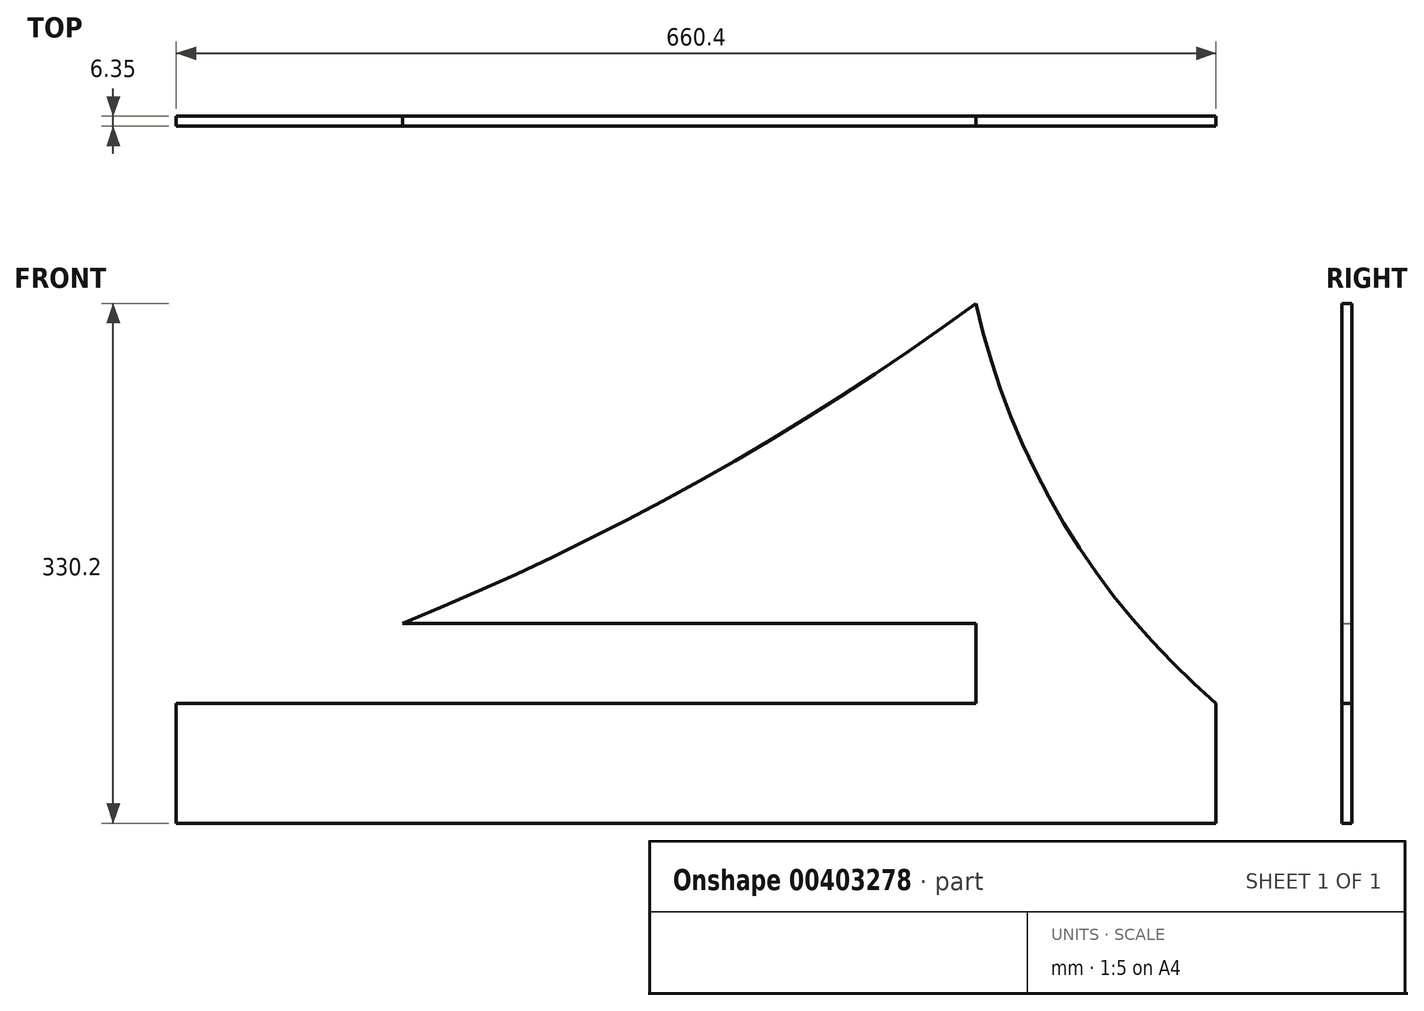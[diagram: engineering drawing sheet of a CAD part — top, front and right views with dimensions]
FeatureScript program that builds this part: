
annotation { "Feature Type Name" : "Feature", "Feature Type Description" : "" }
export const myFeature = defineFeature(function(context is Context, id is Id, definition is map)
    precondition{}
    {
        {
            var Q0;
            Q0=qCreatedBy(makeId("Front.planeOp"),FACE);
            var sketch = newSketch(context, id + "F0", { "sketchPlane" : qUnion([Q0])});
            skLineSegment(sketch, "E0.bottom", {"start": v(0, 0) * mm, "end": v(203.2, 0) * mm});
            skLineSegment(sketch, "E0.top", {"start": v(0, 76.2) * mm, "end": v(203.2, 76.2) * mm});
            skLineSegment(sketch, "E0.left", {"start": v(0, 0) * mm, "end": v(0, 76.2) * mm});
            skLineSegment(sketch, "E0.right", {"start": v(203.2, 0) * mm, "end": v(203.2, 76.2) * mm});
            skLineSegment(sketch, "E1.bottom", {"start": v(0, 0) * mm, "end": v(508, 0) * mm});
            skLineSegment(sketch, "E1.top", {"start": v(0, 254) * mm, "end": v(508, 254) * mm});
            skLineSegment(sketch, "E1.left", {"start": v(0, 0) * mm, "end": v(0, 254) * mm});
            skLineSegment(sketch, "E1.right", {"start": v(508, 0) * mm, "end": v(508, 254) * mm});
            skLineSegment(sketch, "E2.bottom", {"start": v(0, 0) * mm, "end": v(609.6, 0) * mm});
            skLineSegment(sketch, "E2.top", {"start": v(0, 50.8) * mm, "end": v(609.6, 50.8) * mm});
            skLineSegment(sketch, "E2.left", {"start": v(0, 0) * mm, "end": v(0, 50.8) * mm});
            skLineSegment(sketch, "E2.right", {"start": v(609.6, 0) * mm, "end": v(609.6, 50.8) * mm});
            skLineSegment(sketch, "E3", {"start": v(0, 0) * mm, "end": v(660.4, 0) * mm});
            skPoint(sketch, "E3.endSnap0", {"position": v(254, 0) * mm});
            skLineSegment(sketch, "E4.bottom", {"start": v(660.4, 0) * mm, "end": v(0, 0) * mm});
            skLineSegment(sketch, "E4.top", {"start": v(660.4, -76.2) * mm, "end": v(0, -76.2) * mm});
            skLineSegment(sketch, "E4.left", {"start": v(660.4, 0) * mm, "end": v(660.4, -76.2) * mm});
            skLineSegment(sketch, "E4.right", {"start": v(0, 0) * mm, "end": v(0, -76.2) * mm});
            skCircle(sketch, "E5", {"center": v(-488.95, 1612.9) * mm, "radius": 1685.38 * mm});
            skCircle(sketch, "E6", {"center": v(965.2, 355.6) * mm, "radius": 468.35 * mm});
            skSolve(sketch);
        }
        {
            var Q0;
            {var subQ0=sQuery(id+"F0.wireOp",EDGE,"E4.bottom");var subQ1=sQuery(id+"F0.wireOp",EDGE,"E0.right");var subQ2=makeQuery(id+"F0.imprint","INTERSECT",VERTEX,{"derivedFrom":[subQ1,subQ0]});Q0=makeQuery(id+"F0.imprint","IMPRINT",FACE,{"disambiguationData":[TD([[makeQuery(id+"F0.imprint","IMPRINT",EDGE,{"disambiguationData":[TD([[subQ2,-1.0]])],"derivedFrom":subQ1}),1.0]])]});}
            var Q1;
            {var subQ1=sQuery(id+"F0.wireOp",EDGE,"E0.right");var subQ3=sQuery(id+"F0.wireOp",EDGE,"E2.top");var subQ4=makeQuery(id+"F0.imprint","INTERSECT",VERTEX,{"derivedFrom":[subQ1,subQ3]});Q1=makeQuery(id+"F0.imprint","IMPRINT",FACE,{"disambiguationData":[TD([[makeQuery(id+"F0.imprint","IMPRINT",EDGE,{"disambiguationData":[TD([[subQ4,1.0]])],"derivedFrom":subQ3}),1.0]])]});}
            var Q2;
            {var subQ1=sQuery(id+"F0.wireOp",EDGE,"E0.right");var subQ3=sQuery(id+"F0.wireOp",EDGE,"E2.top");var subQ4=makeQuery(id+"F0.imprint","INTERSECT",VERTEX,{"derivedFrom":[subQ1,subQ3]});Q2=makeQuery(id+"F0.imprint","IMPRINT",FACE,{"disambiguationData":[TD([[makeQuery(id+"F0.imprint","IMPRINT",EDGE,{"disambiguationData":[TD([[subQ4,-1.0]])],"derivedFrom":subQ3}),1.0]])]});}
            var Q3;
            {var subQ1=sQuery(id+"F0.wireOp",EDGE,"E1.right");var subQ3=sQuery(id+"F0.wireOp",EDGE,"E2.top");var subQ4=makeQuery(id+"F0.imprint","INTERSECT",VERTEX,{"derivedFrom":[subQ1,subQ3]});Q3=makeQuery(id+"F0.imprint","IMPRINT",FACE,{"disambiguationData":[TD([[makeQuery(id+"F0.imprint","IMPRINT",EDGE,{"disambiguationData":[TD([[subQ4,-1.0]])],"derivedFrom":subQ3}),1.0]])]});}
            var Q4;
            {var subQ5=sQuery(id+"F0.wireOp",EDGE,"E2.right");Q4=makeQuery(id+"F0.imprint","IMPRINT",FACE,{"disambiguationData":[TD([[makeQuery(id+"F0.imprint","IMPRINT",EDGE,{"derivedFrom":subQ5}),1.0]])]});}
            var Q5;
            {var subQ0=sQuery(id+"F0.wireOp",EDGE,"E4.bottom");var subQ1=sQuery(id+"F0.wireOp",EDGE,"E0.right");var subQ2=makeQuery(id+"F0.imprint","INTERSECT",VERTEX,{"derivedFrom":[subQ1,subQ0]});Q5=makeQuery(id+"F0.imprint","IMPRINT",FACE,{"disambiguationData":[TD([[makeQuery(id+"F0.imprint","IMPRINT",EDGE,{"disambiguationData":[TD([[subQ2,-1.0]])],"derivedFrom":subQ1}),-1.0]])]});}
            var Q6;
            {var subQ0=sQuery(id+"F0.wireOp",EDGE,"E2.right");Q6=makeQuery(id+"F0.imprint","IMPRINT",FACE,{"disambiguationData":[TD([[makeQuery(id+"F0.imprint","IMPRINT",EDGE,{"derivedFrom":subQ0}),-1.0]])]});}
            var Q7;
            Q7=makeQuery(id+"F0.imprint","IMPRINT",FACE,{"disambiguationData":[TD([[makeQuery(id+"F0.imprint","IMPRINT",EDGE,{"derivedFrom":sQuery(id+"F0.wireOp",EDGE,"E4.top")}),-1.0]])]});
            extrude(context, id + "F1", {"entities" : qUnion([Q0, Q1, Q2, Q3, Q4, Q5, Q6, Q7]), "depth" : 6.35 * mm});
        }
    });
